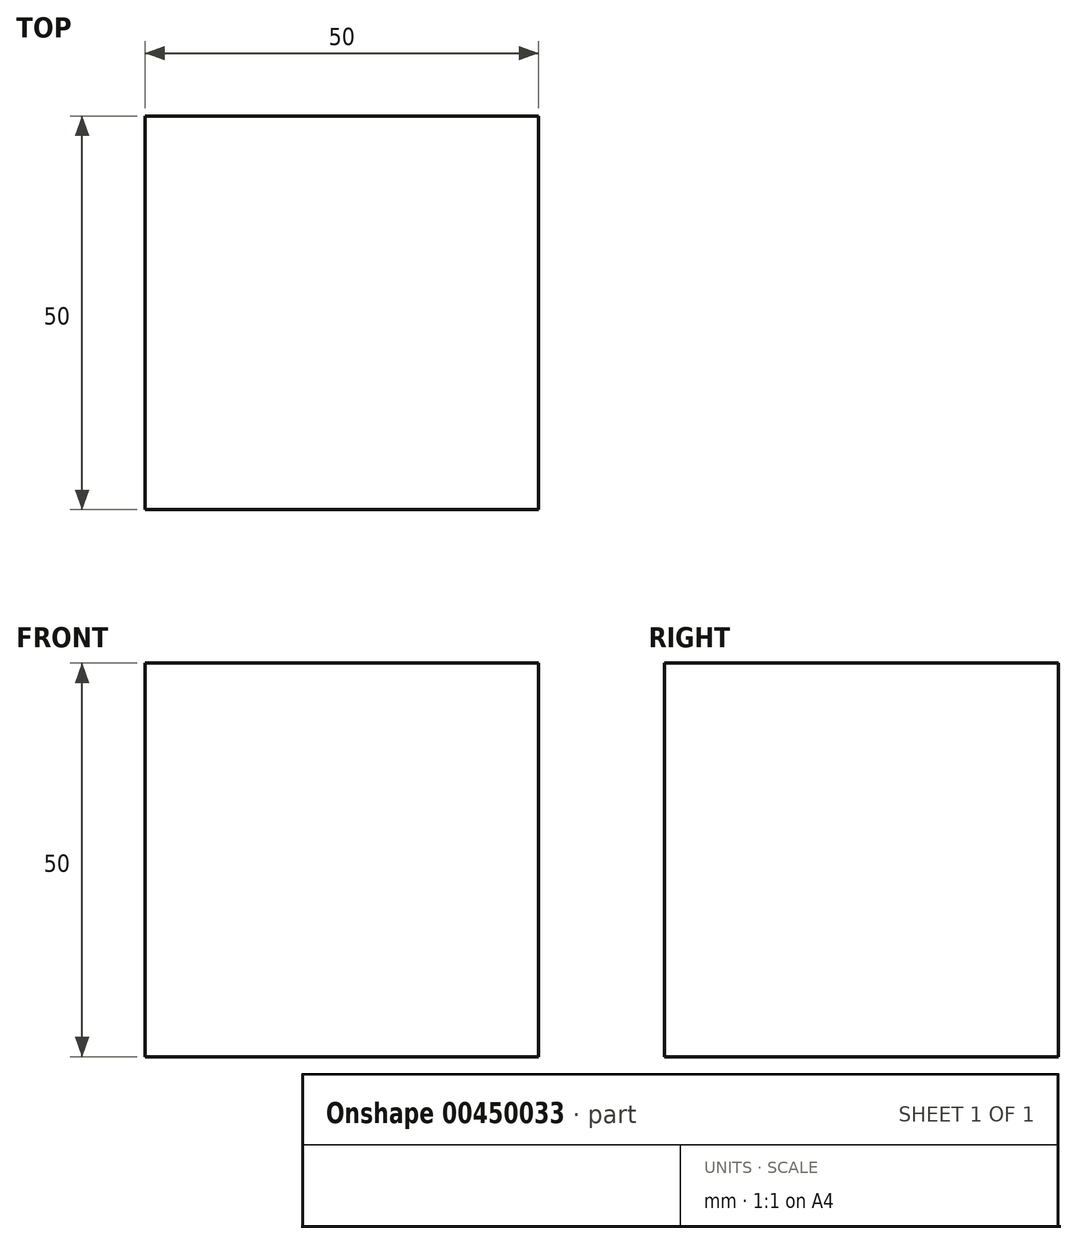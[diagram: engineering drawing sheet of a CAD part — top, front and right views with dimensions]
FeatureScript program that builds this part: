
annotation { "Feature Type Name" : "Feature", "Feature Type Description" : "" }
export const myFeature = defineFeature(function(context is Context, id is Id, definition is map)
    precondition{}
    {
        {
            var Q0;
            Q0=qCreatedBy(makeId("Top.planeOp"),FACE);
            var sketch = newSketch(context, id + "F0", { "sketchPlane" : qUnion([Q0])});
            skLineSegment(sketch, "E0.bottom", {"start": v(-25, -25) * mm, "end": v(25, -25) * mm});
            skLineSegment(sketch, "E0.top", {"start": v(-25, 25) * mm, "end": v(25, 25) * mm});
            skLineSegment(sketch, "E0.left", {"start": v(-25, -25) * mm, "end": v(-25, 25) * mm});
            skLineSegment(sketch, "E0.right", {"start": v(25, -25) * mm, "end": v(25, 25) * mm});
            skPoint(sketch, "E0.middle", {"position": v(0, 0) * mm});
            skSolve(sketch);
        }
        {
            var Q0;
            Q0 = qSketchRegion(id + "F0", true);
            extrude(context, id + "F1", {"entities" : qUnion([Q0]), "depth" : 50 * mm});
        }
    });
